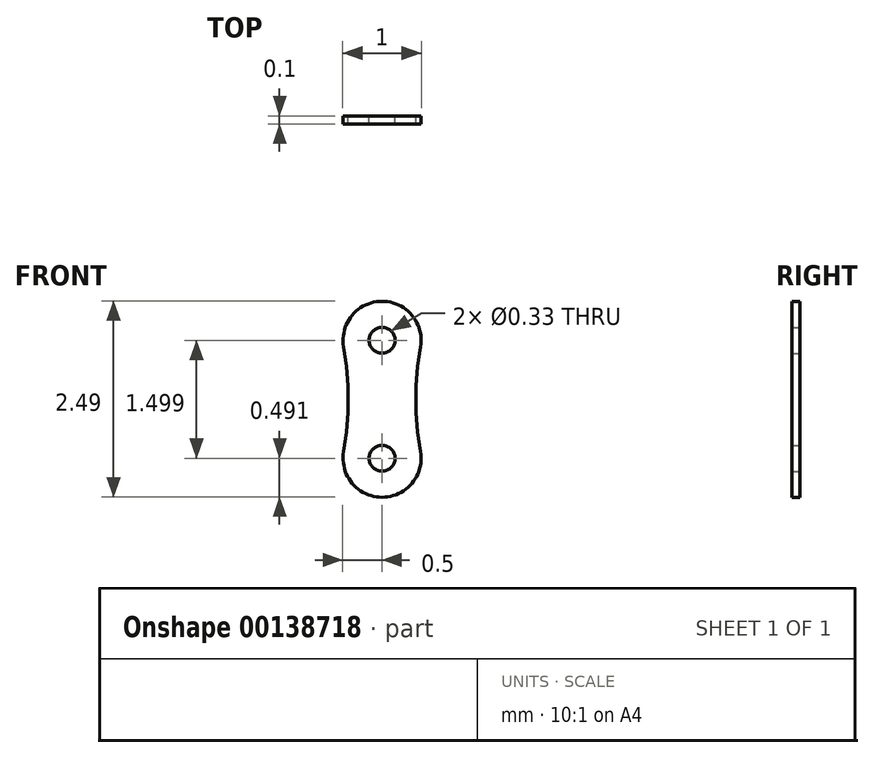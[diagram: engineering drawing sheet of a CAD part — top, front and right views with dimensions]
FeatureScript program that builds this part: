
annotation { "Feature Type Name" : "Feature", "Feature Type Description" : "" }
export const myFeature = defineFeature(function(context is Context, id is Id, definition is map)
    precondition{}
    {
        {
            var Q0;
            Q0=qCreatedBy(makeId("Front.planeOp"),FACE);
            var sketch = newSketch(context, id + "F0", { "sketchPlane" : qUnion([Q0])});
            skCircle(sketch, "E0", {"center": v(0, 0) * mm, "radius": 0.5 * mm});
            skCircle(sketch, "E1", {"center": v(0, -1.5) * mm, "radius": 0.5 * mm});
            skArc(sketch, "E2", {"start": v(-0.49, -1.41) * mm, "mid": v(-0.43, -0.75) * mm, "end": v(-0.49, -0.09) * mm});
            skArc(sketch, "E3", {"start": v(0.49, -0.09) * mm, "mid": v(0.43, -0.75) * mm, "end": v(0.49, -1.41) * mm});
            skCircle(sketch, "E4", {"center": v(0, 0) * mm, "radius": 0.17 * mm});
            skCircle(sketch, "E5", {"center": v(0, -1.5) * mm, "radius": 0.17 * mm});
            skSolve(sketch);
        }
        {
            var Q0;
            Q0=makeQuery(id+"F0.imprint","IMPRINT",FACE,{"disambiguationData":[TD([[makeQuery(id+"F0.imprint","IMPRINT",EDGE,{"derivedFrom":sQuery(id+"F0.wireOp",EDGE,"E4")}),-1.0]])]});
            var Q1;
            {var subQ0=sQuery(id+"F0.wireOp",EDGE,"E2");Q1=makeQuery(id+"F0.imprint","IMPRINT",FACE,{"disambiguationData":[TD([[makeQuery(id+"F0.imprint","IMPRINT",EDGE,{"derivedFrom":subQ0}),-1.0]])]});}
            var Q2;
            Q2=makeQuery(id+"F0.imprint","IMPRINT",FACE,{"disambiguationData":[TD([[makeQuery(id+"F0.imprint","IMPRINT",EDGE,{"derivedFrom":sQuery(id+"F0.wireOp",EDGE,"E5")}),-1.0]])]});
            extrude(context, id + "F1", {"entities" : qUnion([Q0, Q1, Q2]), "depth" : 0.1 * mm});
        }
    });
